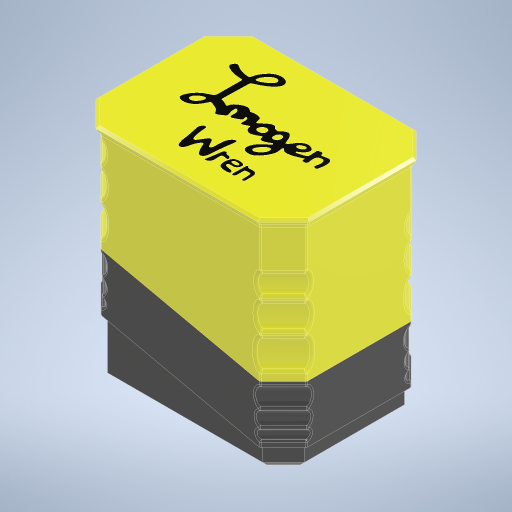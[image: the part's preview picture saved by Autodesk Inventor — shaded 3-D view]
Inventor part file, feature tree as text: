
AUTODESK INVENTOR PART (.ipt)
format: ipt  version: 2024.1 (Build 281209000, 209)  size: 3,330,048 bytes
history: native  units: mm
features: sketch x36, projected_geometry x35, extrude x33, chamfer x20, fillet x16, plane x5, other x4, sweep x1, revolve x1, pattern_linear x1
ambient origin geometry x8: Origin, YZ Plane, XZ Plane, XY Plane, X Axis, Y Axis, Z Axis, Center Point
bodies: Body1 (feature_tree), Body2 (feature_tree), Body3 (feature_tree)
feature tree (152):
  other  "transmitter"
  extrude  "Extrusion1"  Depth=90.6mm
  sweep  "Sweep2"
  chamfer  "Chamfer1"  Distance=14.0mm
  chamfer  "Chamfer2"  [1 undecoded]
  chamfer  "Chamfer3"  Distance=80.0mm Angle=45.0deg
  chamfer  "Chamfer4"  Distance=1.0mm Angle=45.0deg
  chamfer  "Chamfer5"  Distance=9.5mm Angle=45.0deg
  chamfer  "Chamfer6"  Distance=1.0mm Angle=45.0deg
  chamfer  "Chamfer7"  Distance=1.0mm Angle=45.0deg
  extrude  "Extrusion2"  Depth=1.0mm TaperAngle=45.0deg
  extrude  "Extrusion3"  Depth=24.3mm
  plane  "Work Plane1"
  revolve  "Revolution1"  [1 undecoded]
  fillet  "Fillet1"  Radius=13.5mm
  fillet  "Fillet2"  Radius=24.22mm
  fillet  "Fillet3"  Radius=3.175mm
  fillet  "Fillet4"  Radius=2.05mm
  extrude  "Extrusion5"  Depth=2.3mm
  fillet  "Fillet5"  Radius=3.06mm
  extrude  "Extrusion6"  Depth=0.853mm
  extrude  "Extrusion7"  Depth=0.5mm
  pattern_linear  "Rectangular Pattern1"  Count1=2 Spacing1=28.0mm
  extrude  "Extrusion9"  Depth=7.0mm
  extrude  "Extrusion10"  Depth=3.0mm
  extrude  "Extrusion11"  Depth=2.0mm
  extrude  "Extrusion12"  Depth=61.5mm TaperAngle=0.0deg
  chamfer  "Chamfer9"  Distance=30.0mm
  chamfer  "Chamfer10"  Distance=3.0mm
  extrude  "Extrusion13"  Depth=10.0mm
  extrude  "Extrusion17"  Depth=10.0mm
  extrude  "Extrusion18"  Depth=10.0mm
  extrude  "Extrusion19"  Depth=10.0mm
  extrude  "Extrusion14"  Depth=10.0mm
  extrude  "Extrusion20"  Depth=10.0mm
  extrude  "Extrusion21"  Depth=10.0mm
  extrude  "Extrusion22"  Depth=10.0mm
  extrude  "Extrusion15"  Depth=1.6mm TaperAngle=0.0deg
  extrude  "Extrusion23"  Depth=1.6mm TaperAngle=0.0deg
  extrude  "Extrusion24"  Depth=10.0mm TaperAngle=45.0deg
  extrude  "Extrusion25"  Depth=10.0mm TaperAngle=45.0deg
  chamfer  "Chamfer11"  Distance=2.0mm
  extrude  "Extrusion26"  Depth=1.6mm TaperAngle=0.0deg
  extrude  "Extrusion27"  Depth=1.6mm TaperAngle=0.0deg
  chamfer  "Chamfer12"  Distance=4.0mm
  fillet  "Fillet6"  Radius=54.12mm
  fillet  "Fillet7"  Radius=15.0mm
  fillet  "Fillet8"  Radius=15.0mm
  plane  "Work Plane3"
  plane  "Work Plane4"
  sketch  "Sketch37"  dims[d74=21.5mm d75=0.0mm]
  extrude  "Extrusion28"  Depth=10.0mm TaperAngle=0.0deg
  extrude  "Extrusion29"  Depth=10.0mm TaperAngle=0.0deg
  plane  "Work Plane5"
  plane  "Work Plane6"
  extrude  "Extrusion32"  Depth=10.0mm TaperAngle=0.0deg
  extrude  "Extrusion30"  Depth=10.0mm TaperAngle=0.0deg
  extrude  "Extrusion31"  Depth=10.0mm TaperAngle=0.0deg
  extrude  "Extrusion33"  Depth=10.0mm TaperAngle=0.0deg
  chamfer  "Chamfer13"  Distance=10.0mm
  chamfer  "Chamfer14"  Distance=3.0mm Angle=45.0deg
  extrude  "Extrusion34"  Depth=1.6mm TaperAngle=0.0deg
  fillet  "Fillet9"  Radius=1.5mm
  fillet  "Fillet10"  Radius=2.5mm
  chamfer  "Chamfer15"  Distance=1.0mm Angle=45.0deg
  chamfer  "Chamfer16"  Distance=1.5mm
  fillet  "Fillet11"  Radius=2.0mm
  fillet  "Fillet12"  Radius=1.0mm
  chamfer  "Chamfer17"  Distance=6.0mm
  extrude  "Extrusion35"  Depth=10.0mm
  fillet  "Fillet13"  Radius=1.8mm
  chamfer  "Chamfer18"  Distance=5.0mm
  fillet  "Fillet14"  Radius=14.0mm
  fillet  "Fillet15"  Radius=1.6mm
  chamfer  "Chamfer19"  Distance=12.0mm
  chamfer  "Chamfer20"  Distance=1.4mm
  chamfer  "Chamfer21"  Distance=4.0mm
  fillet  "Fillet16"  Radius=6.0mm
  extrude  "Extrusion36"  Depth=1.6mm
  sketch  "Sketch1"  dims[d0=43.3mm d1=90.6mm]
  sketch  "Sketch2"  dims[d2=43.3mm d3=6.3mm]
  sketch  "Sketch3"  dims[d4=8.0mm]
  projected_geometry  "Projected Loop1"
  sketch  "Sketch4"  dims[d5=6.5mm]
  sketch  "Sketch5"  dims[d6=7.8mm d7=14.0mm d8=0.0mm]
  other  "Work Point1"
  sketch  "Sketch7"  dims[d9=1.85mm]
  sketch  "Sketch8"  dims[d10=1.85mm]
  sketch  "Sketch9"  dims[d11=10.3mm d14=0.0mm d15=0.0mm d16=80.0mm d17=1.0mm d18=45.0deg d19=1.0mm d20=80.0mm d21=45.0deg d22=9.5mm d23=80.0mm d24=45.0deg d25=1.0mm d26=80.0mm d27=45.0deg d28=1.0mm d29=80.0mm d30=45.0deg]
  sketch  "Sketch10"  dims[d31=1.0mm d32=12.0mm d33=45.0deg d34=1.0mm d35=12.0mm d36=45.0deg]
  sketch  "Sketch13"  dims[d37=11.2mm d38=24.3mm]
  other  "body-case"
  sketch  "Sketch14"  dims[d39=14.7mm d40=0.0mm d41=12.26mm d42=13.5mm d43=0.0mm d50=24.22mm d51=3.175mm d52=2.05mm]
  projected_geometry  "Projected Loop15"
  projected_geometry  "Projected Loop16"
  projected_geometry  "Projected Loop17"
  projected_geometry  "Projected Loop18"
  projected_geometry  "Projected Loop19"
  projected_geometry  "Projected Loop20"
  projected_geometry  "Projected Loop21"
  projected_geometry  "Projected Loop22"
  sketch  "Sketch15"  dims[d53=1.38mm d54=2.3mm d55=3.06mm]
  projected_geometry  "Projected Loop23"
  sketch  "Sketch16"  dims[d56=3.54mm d57=0.853mm]
  projected_geometry  "Projected Loop24"
  sketch  "Sketch17"  dims[d58=90.0deg d59=0.5mm]
  projected_geometry  "Projected Loop25"
  sketch  "Sketch18"  dims[d60=0.8mm]
  projected_geometry  "Projected Loop26"
  sketch  "Sketch20"  dims[d61=0.8mm]
  projected_geometry  "Projected Loop27"
  other  "lid"
  sketch  "Sketch22"  dims[d62=0.8mm]
  projected_geometry  "Projected Loop29"
  projected_geometry  "Projected Loop30"
  sketch  "Sketch24"  dims[d63=6.8mm]
  projected_geometry  "Projected Loop31"
  sketch  "Sketch26"  dims[d64=10.1mm]
  projected_geometry  "Projected Loop32"
  sketch  "Sketch27"  dims[d65=4.3mm]
  projected_geometry  "Projected Loop33"
  sketch  "Sketch28"  dims[d66=18.5mm]
  projected_geometry  "Projected Loop34"
  projected_geometry  "Projected Loop35"
  projected_geometry  "Projected Loop36"
  projected_geometry  "Projected Loop37"
  sketch  "Sketch29"  dims[d67=30.6mm]
  projected_geometry  "Projected Loop38"
  sketch  "Sketch30"  dims[d68=1.6mm d69=0.0mm]
  projected_geometry  "Projected Loop39"
  sketch  "Sketch31"  dims[d70=0.8mm]
  projected_geometry  "Projected Loop40"
  projected_geometry  "Projected Loop41"
  projected_geometry  "Projected Loop42"
  projected_geometry  "Projected Loop43"
  sketch  "Sketch32"  dims[d71=5.5mm]
  projected_geometry  "Projected Loop44"
  sketch  "Sketch34"  dims[d72=10.5mm]
  projected_geometry  "Projected Loop45"
  sketch  "Sketch35"  dims[d73=2.8mm]
  projected_geometry  "Projected Loop46"
  sketch  "Sketch38"  dims[d76=3.2mm]
  sketch  "Sketch39"  dims[d77=10.0mm d78=0.0mm d79=20.0mm d81=28.0mm]
  sketch  "Sketch40"  dims[d88=7.0mm d89=7.0mm]
  sketch  "Sketch41"  dims[d90=8.0mm d91=3.0mm]
  sketch  "Sketch42"  dims[d92=3.0mm d93=0.0mm d94=2.0mm]
  projected_geometry  "Projected Loop47"
  sketch  "Sketch44"  dims[d96=2.0mm d97=61.5mm d98=0.0mm]
  projected_geometry  "Projected Loop48"
  sketch  "Sketch45"  dims[d100=4.0mm]
  sketch  "Sketch46"  dims[d101=4.0mm d102=30.0mm d103=3.0mm d104=10.0mm d105=10.0mm d106=10.0mm d107=10.0mm d108=10.0mm d109=10.0mm d110=10.0mm d111=10.0mm d112=61.5mm d113=0.0mm d114=3.0mm d115=0.0mm d116=10.0mm d117=2.0mm d118=45.0deg d119=10.0mm d120=2.0mm d121=45.0deg d122=2.0mm d123=15.0mm d124=0.0mm d125=25.0mm d126=0.0mm d127=4.0mm d128=54.12mm d129=0.0mm d133=15.0mm d134=0.0mm d135=15.0mm d136=0.0mm d137=10.0mm d138=0.0mm d139=10.0mm d140=0.0mm d141=10.0mm d142=0.0mm d143=10.0mm d144=0.0mm d145=10.0mm d146=0.0mm d147=10.0mm d148=0.0mm d149=10.0mm d150=0.0mm d151=3.0mm d152=2.0mm d153=45.0deg d154=2.0mm d155=0.0mm d156=1.5mm d157=2.5mm d158=0.0mm d159=1.0mm d160=2.0mm d161=45.0deg d162=1.5mm d163=2.0mm d164=1.0mm d165=6.0mm d166=10.0mm d167=1.8mm d168=5.0mm d169=14.0mm d170=1.6mm d171=12.0mm d172=1.4mm d173=4.0mm d174=6.0mm d175=4.0mm d176=1.8mm d177=3.0mm d178=8.0mm d179=6.0mm d180=1.6mm d181=1.4mm d182=2.0mm d183=0.0mm d184=0.0mm d185=6.0mm d186=10.0mm d187=1.8mm d188=5.0mm d189=14.0mm d190=1.6mm d191=12.0mm d192=1.4mm d193=4.0mm d194=6.0mm d195=4.0mm d196=1.8mm d197=3.0mm d198=8.0mm d199=6.0mm d200=1.6mm d201=1.4mm d202=2.0mm d203=0.0mm d204=0.0mm d205=6.0mm d206=10.0mm d207=1.8mm d208=5.0mm d209=14.0mm d210=1.6mm d211=12.0mm d212=1.4mm d213=4.0mm d214=6.0mm d215=4.0mm d216=1.8mm d217=3.0mm d218=8.0mm d219=6.0mm d220=1.6mm d221=1.4mm d222=2.0mm d223=0.0mm d224=0.0mm d225=6.0mm d226=10.0mm d227=1.8mm d228=5.0mm d229=14.0mm d230=1.6mm d231=12.0mm d232=1.4mm d233=4.0mm d234=6.0mm d235=4.0mm d236=1.8mm d237=3.0mm d238=8.0mm d239=6.0mm d240=1.6mm d241=1.4mm d242=2.0mm d243=0.0mm d244=0.0mm d245=0.02mm d246=0.0mm d247=0.35mm d248=0.35mm d249=0.02mm d250=0.0mm d251=1.5mm d252=2.0mm d253=45.0deg d254=3.0mm d255=2.0mm d256=45.0deg d257=2.0mm d258=2.0mm d259=1.0mm d260=0.0mm d261=2.0mm d262=2.0mm d263=45.0deg d264=2.0mm d265=2.0mm d266=45.0deg d267=1.0mm d268=1.0mm d269=3.0mm d270=2.0mm d271=45.0deg d272=24.0mm d273=10.15mm d274=9.85mm d275=4.0mm d276=4.0mm d277=43.0mm d278=0.0mm d279=2.0mm d280=1.9mm d281=2.0mm d282=45.0deg d283=2.1mm d284=2.1mm d285=0.5mm d286=2.0mm d287=45.0deg d288=2.0mm d289=2.0mm d290=45.0deg d291=2.0mm d292=2.0mm d293=45.0deg d294=2.0mm d295=1.0mm d296=27.0mm d297=0.0mm]
  projected_geometry  "Projected Loop49"
note: 2 required parameter values undecoded (feature->parameter linkage not recoverable at this tier; creation-order binding heuristic only, values carry confidence <= 0.55)